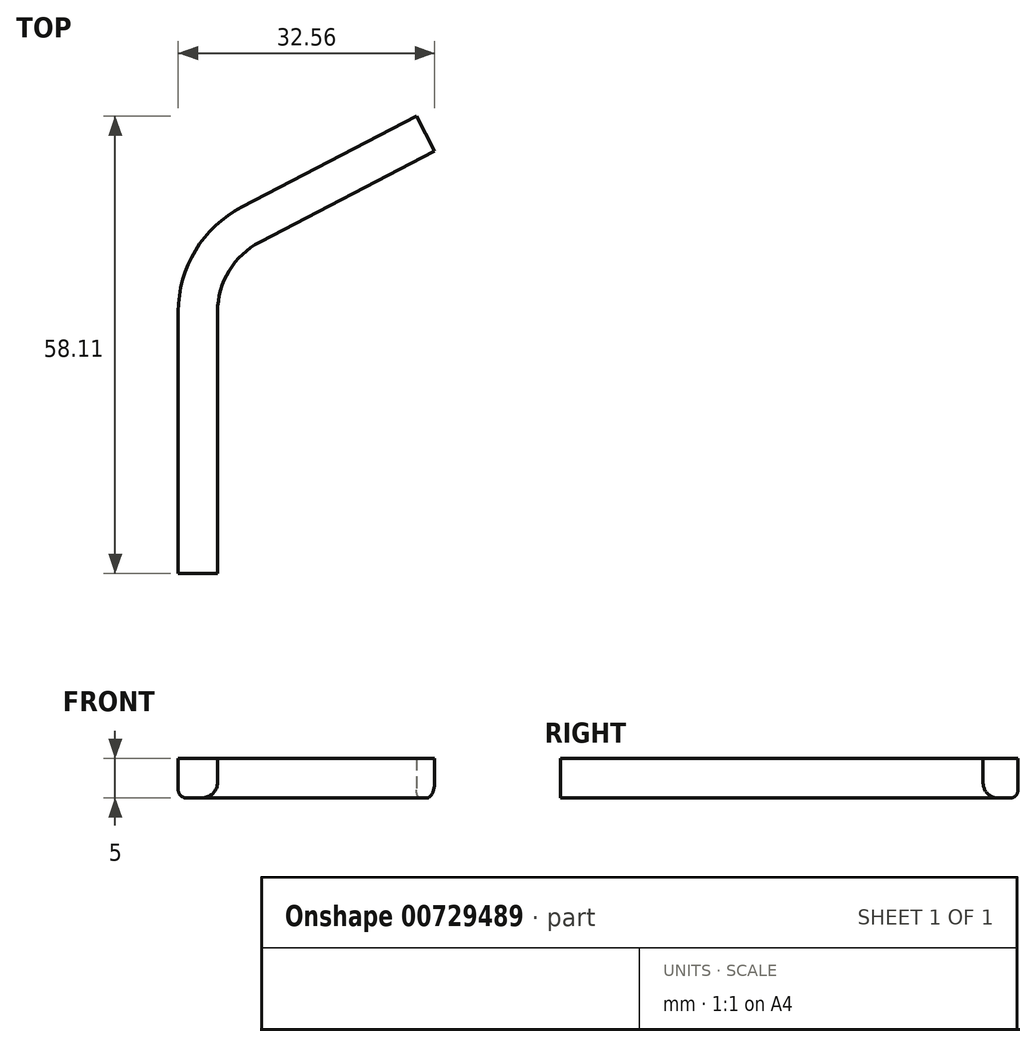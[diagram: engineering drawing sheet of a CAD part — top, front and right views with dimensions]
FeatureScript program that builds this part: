
annotation { "Feature Type Name" : "Feature", "Feature Type Description" : "" }
export const myFeature = defineFeature(function(context is Context, id is Id, definition is map)
    precondition{}
    {
        {
            var Q0;
            Q0=qCreatedBy(makeId("Top.planeOp"),FACE);
            var sketch = newSketch(context, id + "F0", { "sketchPlane" : qUnion([Q0])});
            skLineSegment(sketch, "E0", {"start": v(-55.5, 0) * mm, "end": v(-60.5, 0) * mm});
            skLineSegment(sketch, "E1", {"start": v(-60.5, 0) * mm, "end": v(-60.5, 33.26) * mm});
            skLineSegment(sketch, "E2", {"start": v(0, 0) * mm, "end": v(-30.25, 58.1) * mm, "construction": true});
            skLineSegment(sketch, "E3", {"start": v(-30.25, 58.1) * mm, "end": v(-52.42, 46.56) * mm});
            skLineSegment(sketch, "E4", {"start": v(-27.94, 53.67) * mm, "end": v(-50.12, 42.13) * mm});
            skLineSegment(sketch, "E5", {"start": v(-55.5, 33.26) * mm, "end": v(-55.5, 0) * mm});
            skLineSegment(sketch, "E6", {"start": v(-60.5, 42.36) * mm, "end": v(0, 0) * mm, "construction": true});
            skLineSegment(sketch, "E7", {"start": v(-30.25, 58.1) * mm, "end": v(-27.94, 53.67) * mm});
            skPoint(sketch, "E8.visualSharp", {"position": v(-60.5, 42.36) * mm});
            skArc(sketch, "E8.filletArc", {"start": v(-52.42, 46.56) * mm, "mid": v(-58.32, 41.04) * mm, "end": v(-60.5, 33.26) * mm});
            skPoint(sketch, "E9.visualSharp", {"position": v(-55.5, 39.33) * mm});
            skArc(sketch, "E9.filletArc", {"start": v(-50.12, 42.13) * mm, "mid": v(-54.05, 38.45) * mm, "end": v(-55.5, 33.26) * mm});
            skSolve(sketch);
        }
        {
            var Q0;
            Q0 = qSketchRegion(id + "F0", true);
            extrude(context, id + "F1", {"entities" : qUnion([Q0]), "depth" : 5 * mm, "offsetDistance" : 25 * mm});
        }
        {
            var Q0;
            Q0=makeQuery(id+"F1.opExtrude","CAP_EDGE",EDGE,{"disambiguationData":[OSD([sQuery(id+"F0.wireOp",EDGE,"E5")])],"isStart":true});
            fillet(context, id + "F2", {"entities" : qUnion([Q0]), "radius" : 2 * mm, "tangentPropagation" : true, "allowEdgeOverflow" : false});
        }
        {
            var Q0;
            Q0=makeQuery(id+"F1.opExtrude","CAP_EDGE",EDGE,{"disambiguationData":[OSD([sQuery(id+"F0.wireOp",EDGE,"E1")])],"isStart":true});
            fillet(context, id + "F3", {"entities" : qUnion([Q0]), "radius" : 1 * mm, "tangentPropagation" : true, "allowEdgeOverflow" : false});
        }
    });
